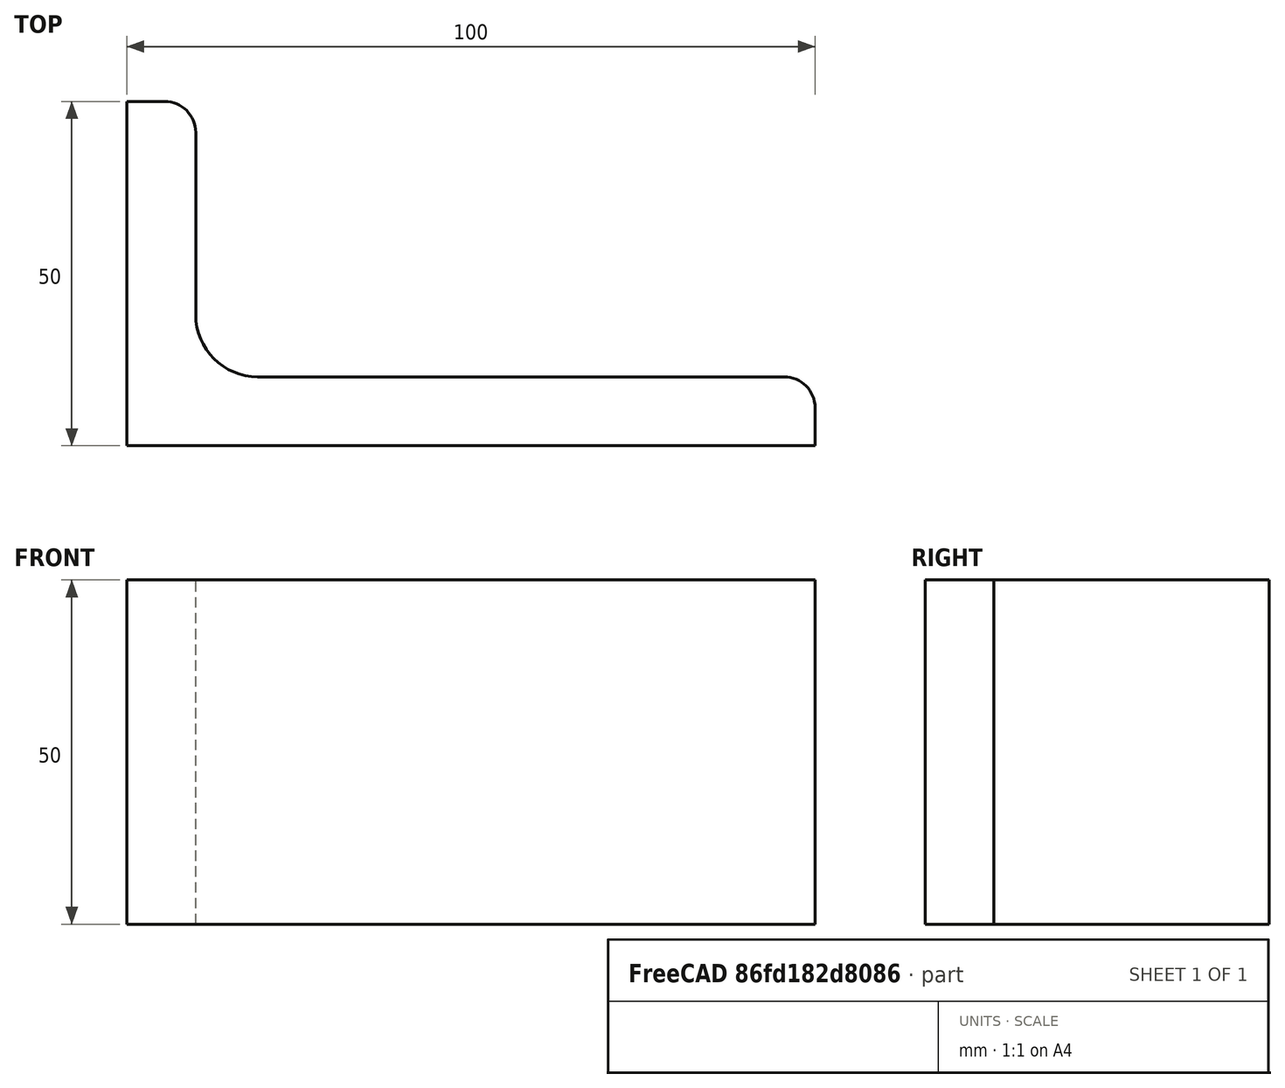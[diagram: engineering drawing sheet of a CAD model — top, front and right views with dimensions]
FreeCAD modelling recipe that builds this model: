
FCSTD DOCUMENT  (FreeCAD 0.15R4671 (Git))
Label: Angle Bar 100x50x10 EN10056 S235JR
License: All rights reserved
LicenseURL: http://en.wikipedia.org/wiki/All_rights_reserved
objects: Sketcher::SketchObject×1, Part::Extrusion×1
note: 2 computed .brp shape members not serialized (recipe doc carries the construction recipe); baked Part::Feature solids carry a one-line shape summary decoded from their .brp

FEATURE [Sketcher::SketchObject] Sketch
  sketch-geometry (9):
    g0: LineSegment StartX=0 StartY=0 StartZ=0 EndX=100 EndY=0 EndZ=0
    g1: LineSegment StartX=100 StartY=0 StartZ=0 EndX=100 EndY=5.5 EndZ=0
    g2: LineSegment StartX=95.5 StartY=10 StartZ=0 EndX=19 EndY=10 EndZ=0
    g3: LineSegment StartX=0 StartY=0 StartZ=0 EndX=0 EndY=50 EndZ=0
    g4: LineSegment StartX=0 StartY=50 StartZ=0 EndX=5.5 EndY=50 EndZ=0
    g5: LineSegment StartX=10 StartY=45.5 StartZ=0 EndX=10 EndY=19 EndZ=0
    g6: ArcOfCircle CenterX=19 CenterY=19 CenterZ=0 NormalX=0 NormalY=0 NormalZ=1 Radius=9 StartAngle=3.14159 EndAngle=4.71239
    g7: ArcOfCircle CenterX=5.5 CenterY=45.5 CenterZ=0 NormalX=0 NormalY=0 NormalZ=1 Radius=4.5 StartAngle=0 EndAngle=1.5708
    g8: ArcOfCircle CenterX=95.5 CenterY=5.5 CenterZ=0 NormalX=0 NormalY=0 NormalZ=1 Radius=4.5 StartAngle=0 EndAngle=1.5708
  constraints (23):
    c: Coincident(g0,g-1)
    c: Horizontal(g0)
    c: Coincident(g1,g0)
    c: Vertical(g1)
    c: Horizontal(g2)
    c: Coincident(g3,g-1)
    c: Vertical(g3)
    c: Coincident(g4,g3)
    c: Horizontal(g4)
    c: Vertical(g5)
    c: Tangent(g5,g6) = -1.5708
    c: Tangent(g2,g6) = 1.5708
    c: Tangent(g4,g7) = 1.5708
    c: Tangent(g5,g7) = 1.5708
    c: Tangent(g2,g8) = -1.5708
    c: Tangent(g1,g8) = -1.5708
    c: DistanceX(g0) = 100
    c: DistanceY(g3) = 50
    c: DistanceY(g0,g2) = 10
    c: DistanceX(g3,g5) = 10
    c: Radius(g6) = 9
    c: Radius(g8) = 4.5
    c: Radius(g7) = 4.5
FEATURE [Part::Extrusion] Extrude  label="Angle Bar 100x50x10 EN10056 S235JR"
  Base = -> Sketch
  Dir = (0,0,50)
  Solid = true
